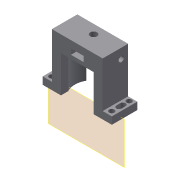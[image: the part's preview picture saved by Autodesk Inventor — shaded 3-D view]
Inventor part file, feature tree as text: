
AUTODESK INVENTOR PART (.ipt)
format: ipt  version: 2019.4 (Build 234330000, 330)  size: 228,864 bytes
history: native  units: mm
features: reference x6, extrude x4, sketch x4, other x3, plane x1, mirror x1, projected_geometry x1
ambient origin geometry x8: Origin, YZ Plane, XZ Plane, XY Plane, X Axis, Y Axis, Z Axis, Center Point
bodies: Solid1 (feature_tree)
feature tree (20):
  plane  "Work Plane1"
  extrude  "Extrusion1"  Depth=4.0mm
  extrude  "Extrusion2"  Depth=25.0mm
  extrude  "Extrusion3"  Depth=6.9mm
  extrude  "Extrusion4"  Depth=5.0mm TaperAngle=0.0deg
  mirror  "Mirror1"
  sketch  "Sketch1"  dims[d0=9.0mm d1=4.0mm]
  reference  "Reference1"
  sketch  "Sketch2"  dims[d2=5.0mm d3=25.0mm]
  reference  "Reference3"
  sketch  "Sketch3"  dims[d6=2.0mm d7=6.9mm]
  projected_geometry  "Projected Loop1"
  sketch  "Sketch4"  dims[d8=2.95mm d9=5.0mm d10=0.0mm d12=10.0mm d13=0.0mm d14=2.9mm d15=10.0mm d16=0.0mm d17=10.0mm d18=0.0mm d19=3.8mm d20=4.0mm d21=2.0mm d22=9.0mm d23=0.0mm]
  reference  "Reference6"
  reference  "Reference7"
  reference  "Reference8"
  reference  "Reference9"
  other  "Assembly_Opentrons_Autofocus_v2.iam"
  other  "01_Slide_camera_v1:1"
  other  "DIN 912 - replaced by DIN EN ISO 4762 M4 x 20:1"
